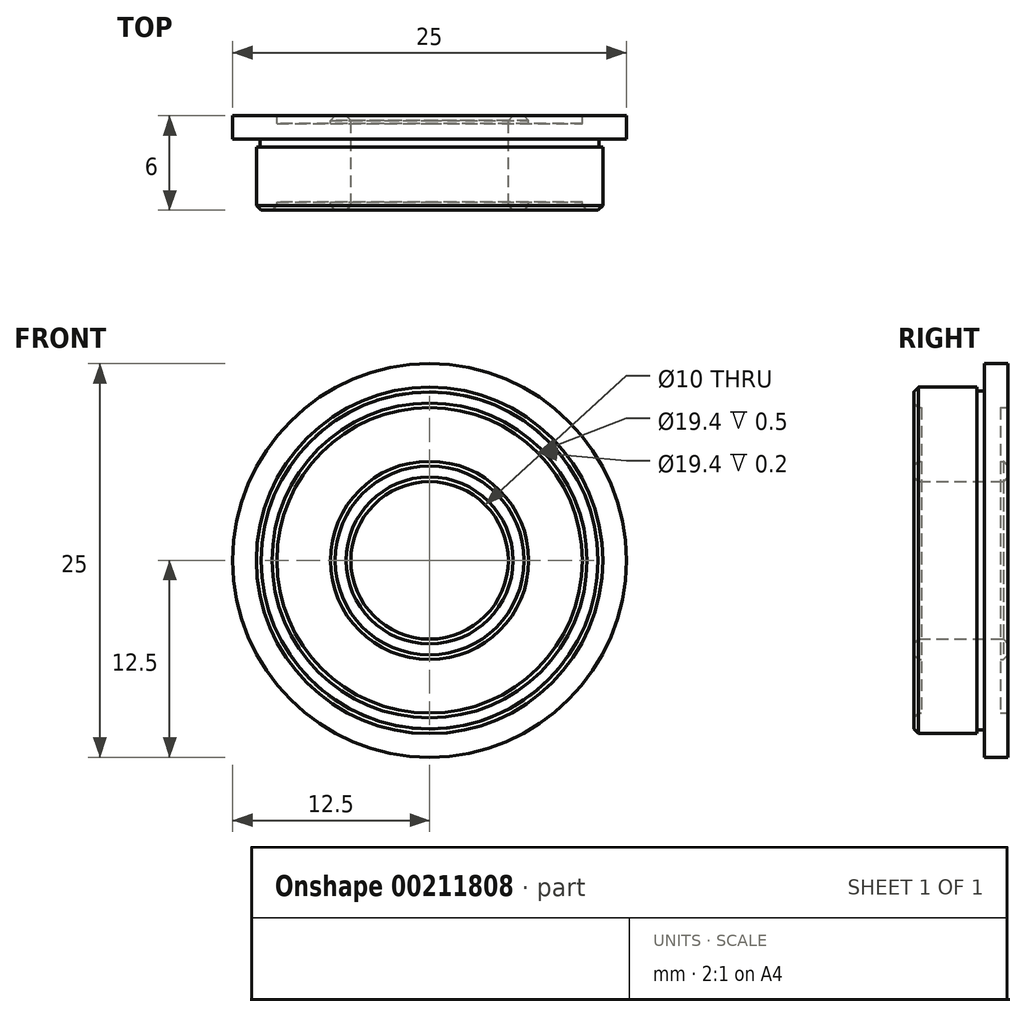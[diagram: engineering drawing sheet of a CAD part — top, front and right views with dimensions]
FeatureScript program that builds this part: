
annotation { "Feature Type Name" : "Feature", "Feature Type Description" : "" }
export const myFeature = defineFeature(function(context is Context, id is Id, definition is map)
    precondition{}
    {
        {
            var Q0;
            Q0=qCreatedBy(makeId("Right.planeOp"),FACE);
            var sketch = newSketch(context, id + "F0", { "sketchPlane" : qUnion([Q0])});
            skLineSegment(sketch, "E0", {"start": v(0, 0) * mm, "end": v(-3.73, 0) * mm, "construction": true});
            skLineSegment(sketch, "E1", {"start": v(0, 0) * mm, "end": v(0, 5) * mm, "construction": true});
            skLineSegment(sketch, "E2", {"start": v(-3, 5) * mm, "end": v(3, 5) * mm});
            skLineSegment(sketch, "E3", {"start": v(3, 5) * mm, "end": v(3, 6.3) * mm});
            skLineSegment(sketch, "E4", {"start": v(3, 6.3) * mm, "end": v(2.5, 6.3) * mm});
            skLineSegment(sketch, "E5", {"start": v(2.5, 6.3) * mm, "end": v(2.5, 9.7) * mm});
            skLineSegment(sketch, "E6", {"start": v(2.5, 9.7) * mm, "end": v(3, 9.7) * mm});
            skLineSegment(sketch, "E7", {"start": v(3, 9.7) * mm, "end": v(3, 12.5) * mm});
            skLineSegment(sketch, "E8", {"start": v(3, 12.5) * mm, "end": v(1.5, 12.5) * mm});
            skLineSegment(sketch, "E9", {"start": v(1, 11) * mm, "end": v(-3, 11) * mm});
            skLineSegment(sketch, "E10.MirrorCS", {"start": v(-3, 6.3) * mm, "end": v(-2.5, 6.3) * mm});
            skLineSegment(sketch, "E11.MirrorCS", {"start": v(-2.5, 9.7) * mm, "end": v(-3, 9.7) * mm});
            skLineSegment(sketch, "E12.MirrorCS", {"start": v(-2.5, 6.3) * mm, "end": v(-2.5, 9.7) * mm});
            skLineSegment(sketch, "E13.MirrorCS", {"start": v(-3, 5) * mm, "end": v(-3, 6.3) * mm});
            skLineSegment(sketch, "E14.MirrorCS", {"start": v(-3, 9.7) * mm, "end": v(-3, 11) * mm});
            skLineSegment(sketch, "E15", {"start": v(1.5, 12.5) * mm, "end": v(1.5, 10.75) * mm});
            skLineSegment(sketch, "E16", {"start": v(1.5, 10.75) * mm, "end": v(1, 10.75) * mm});
            skLineSegment(sketch, "E17", {"start": v(1, 10.75) * mm, "end": v(1, 11) * mm});
            skSolve(sketch);
        }
        {
            var Q0;
            Q0=makeQuery(id+"F0.imprint","IMPRINT",FACE,{"disambiguationData":[TD([[makeQuery(id+"F0.imprint","IMPRINT",EDGE,{"derivedFrom":sQuery(id+"F0.wireOp",EDGE,"E2")}),1.0]])]});
            var Q1;
            Q1=sQuery(id+"F0.wireOp",EDGE,"E0");
            revolve(context, id + "F1", {"entities" : qUnion([Q0]), "axis" : qUnion([Q1]), "revolveType" : RevolveType.FULL});
        }
        {
            var Q0;
            Q0=makeQuery(id+"F1.opRevolve","SWEPT_FACE",FACE,{"disambiguationData":[OSD([sQuery(id+"F0.wireOp",EDGE,"E13.MirrorCS")])]});
            var Q1;
            Q1=makeQuery(id+"F1.opRevolve","SWEPT_FACE",FACE,{"disambiguationData":[OSD([sQuery(id+"F0.wireOp",EDGE,"E14.MirrorCS")])]});
            var Q2;
            Q2=makeQuery(id+"F1.opRevolve","SWEPT_FACE",FACE,{"disambiguationData":[OSD([sQuery(id+"F0.wireOp",EDGE,"E3")])]});
            chamfer(context, id + "F2", {"entities" : qUnion([Q0, Q1, Q2]), "width" : .3 * mm, "tangentPropagation" : true});
        }
    });
